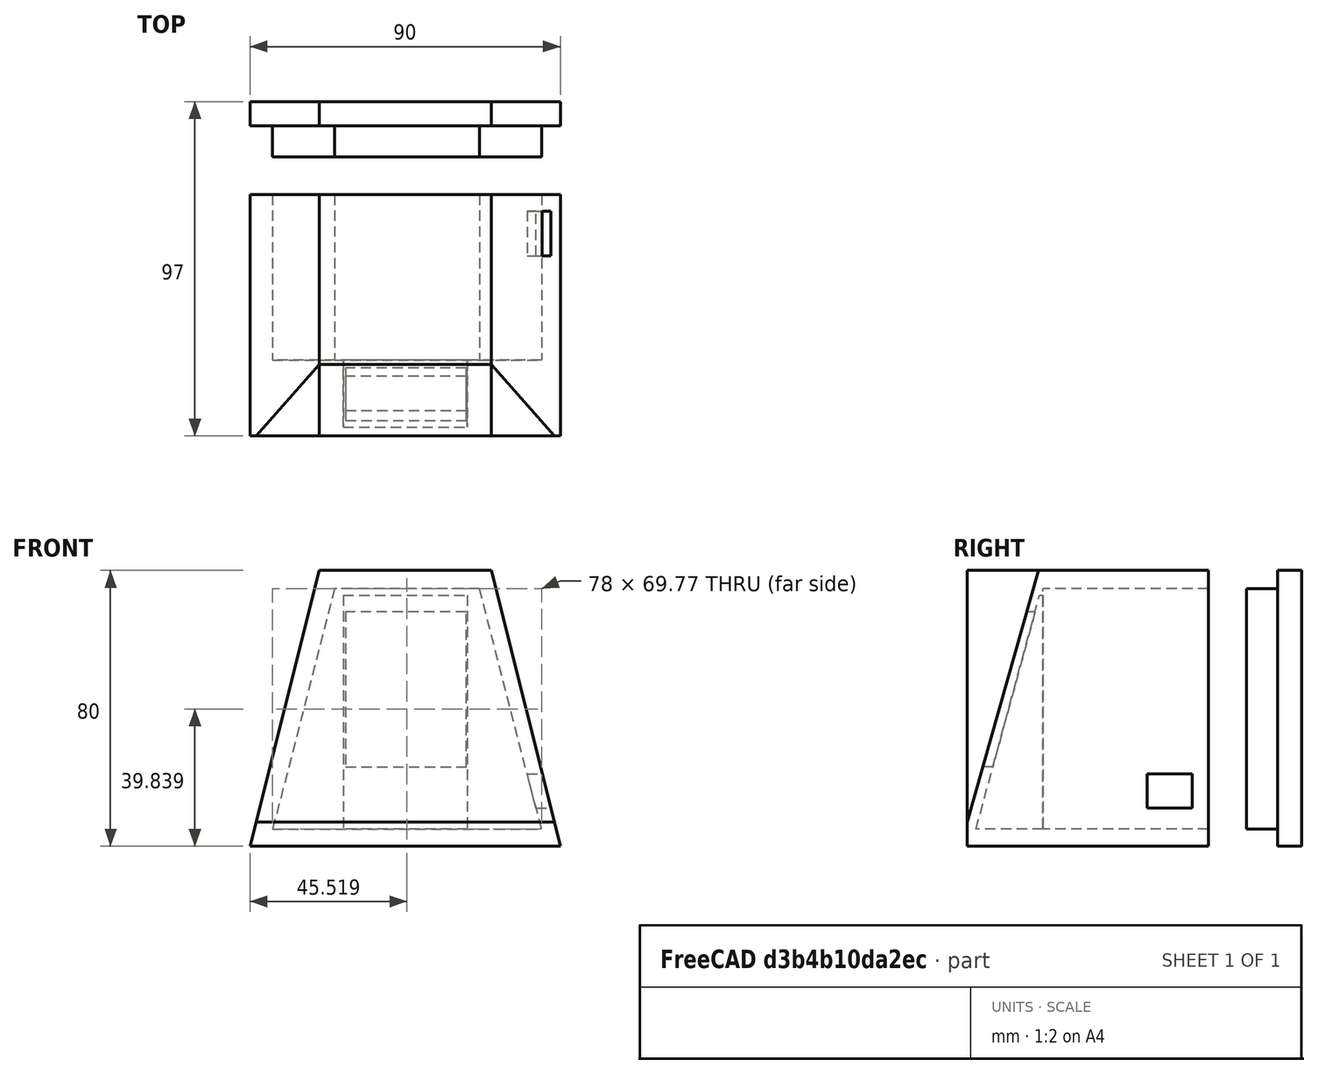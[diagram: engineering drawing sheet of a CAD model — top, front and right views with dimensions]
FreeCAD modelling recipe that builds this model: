
FCSTD DOCUMENT  (FreeCAD 0.19R24415 (Git))
Label: cad_1
License: All rights reserved
LicenseURL: http://en.wikipedia.org/wiki/All_rights_reserved
objects: Sketcher::SketchObject×8, Part::Extrusion×7, Part::Cut×6, Mesh::Feature×2, PartDesign::Pad×1, PartDesign::Body×1, Part::Fuse×1
note: 25 computed .brp shape members not serialized (recipe doc carries the construction recipe); baked Part::Feature solids carry a one-line shape summary decoded from their .brp

FEATURE [Sketcher::SketchObject] Sketch
  FullyConstrained = true
  MapMode = 5
  Placement = pos=(0,0,0) rot=(1,0,0;1.5708rad)
  Support = -> [XZ_Plane]
  sketch-geometry (4):
    g0: LineSegment StartX=0 StartY=0 StartZ=0 EndX=90 EndY=0 EndZ=0
    g1: LineSegment StartX=90 StartY=0 StartZ=0 EndX=70 EndY=80 EndZ=0
    g2: LineSegment StartX=70 StartY=80 StartZ=0 EndX=20 EndY=80 EndZ=0
    g3: LineSegment StartX=20 StartY=80 StartZ=0 EndX=0 EndY=0 EndZ=0
  constraints (11):
    c: Horizontal(g0)
    c: Coincident(g0,g1)
    c: Coincident(g1,g2)
    c: Horizontal(g2)
    c: Coincident(g2,g3)
    c: Coincident(g3,g0)
    c: Equal(g3,g1)
    c: DistanceX(g0,g0) = 90
    c: DistanceX(g2,g2) = 50
    c: Coincident(g0,g-1)
    c: DistanceY(g0,g1) = 80
FEATURE [PartDesign::Pad] Pad
  Direction = (1,1,1)
  Length = 70
  Length2 = 100
  Placement = pos=(0,0,0) rot=(1,0,0;1.5708rad)
  Profile = -> Sketch
  Refine = true
  Type = 0
FEATURE [PartDesign::Body] Body
  Group = -> [Sketch,Pad]
  Origin = -> Origin
  Tip = -> Pad
FEATURE [Sketcher::SketchObject] Sketch001
  FullyConstrained = true
  MapMode = 5
  Placement = pos=(0,0,0) rot=(0.57735,0.57735,0.57735;2.0944rad)
  Support = -> [YZ_Plane]
  sketch-geometry (4):
    g0: LineSegment StartX=-105 StartY=0 StartZ=0 EndX=-105 EndY=95 EndZ=0
    g1: LineSegment StartX=-105 StartY=95 StartZ=0 EndX=-45 EndY=95 EndZ=0
    g2: LineSegment StartX=-45 StartY=95 StartZ=0 EndX=-72 EndY=0 EndZ=0
    g3: LineSegment StartX=-72 StartY=0 StartZ=0 EndX=-105 EndY=0 EndZ=0
  constraints (12):
    c: PointOnObject(g0,g-1)
    c: Vertical(g0)
    c: Coincident(g0,g1)
    c: Horizontal(g1)
    c: Coincident(g1,g2)
    c: PointOnObject(g2,g-1)
    c: Coincident(g2,g3)
    c: Coincident(g3,g0)
    c: DistanceX(g0,g-1) = 105
    c: DistanceX(g1,g1) = 60
    c: DistanceX(g3,g3) = 33
    c: DistanceY(g0,g0) = 95
FEATURE [Part::Extrusion] Extrude
  Base = -> Sketch001
  Dir = (1,-1e-16,1e-16)
  DirMode = 2
  FaceMakerClass = Part::FaceMakerBullseye
  LengthFwd = 100
  LengthRev = 0
  Solid = true
  Symmetric = false
FEATURE [Part::Cut] Cut
  Base = -> Pad
  Refine = true
  Tool = -> Extrude
FEATURE [Sketcher::SketchObject] Sketch002
  FullyConstrained = false
  MapMode = 5
  Placement = pos=(0,0,0) rot=(1,0,0;1.5708rad)
  Support = -> [XZ_Plane]
  sketch-geometry (4):
    g0: LineSegment StartX=6.51919 StartY=4.95552 StartZ=0 EndX=24.5192 EndY=74.7219 EndZ=0
    g1: LineSegment StartX=24.5192 StartY=74.7219 StartZ=0 EndX=66.5192 EndY=74.7219 EndZ=0
    g2: LineSegment StartX=66.5192 StartY=74.7219 StartZ=0 EndX=84.5192 EndY=4.95552 EndZ=0
    g3: LineSegment StartX=84.5192 StartY=4.95552 StartZ=0 EndX=6.51919 EndY=4.95552 EndZ=0
  constraints (9):
    c: Coincident(g0,g1)
    c: Horizontal(g1)
    c: Coincident(g1,g2)
    c: Coincident(g2,g3)
    c: Coincident(g3,g0)
    c: Horizontal(g3)
    c: Equal(g2,g0)
    c: DistanceX(g3,g3) = 78
    c: DistanceX(g1,g1) = 42
FEATURE [Part::Extrusion] Extrude001
  Base = -> Sketch002
  Dir = (0,-1,2e-16)
  DirMode = 2
  FaceMakerClass = Part::FaceMakerBullseye
  LengthFwd = 100
  LengthRev = 0
  Placement = pos=(0,52,0) rot=(0,0,1;0rad)
  Solid = true
  Symmetric = false
FEATURE [Sketcher::SketchObject] Sketch003
  FullyConstrained = false
  MapMode = 5
  Placement = pos=(0,0,0) rot=(1,0,0;1.5708rad)
  sketch-geometry (4):
    g0: LineSegment StartX=6.51919 StartY=4.95552 StartZ=0 EndX=24.5192 EndY=74.7219 EndZ=0
    g1: LineSegment StartX=24.5192 StartY=74.7219 StartZ=0 EndX=66.5192 EndY=74.7219 EndZ=0
    g2: LineSegment StartX=66.5192 StartY=74.7219 StartZ=0 EndX=84.5192 EndY=4.95552 EndZ=0
    g3: LineSegment StartX=84.5192 StartY=4.95552 StartZ=0 EndX=6.51919 EndY=4.95552 EndZ=0
  constraints (9):
    c: Coincident(g0,g1)
    c: Horizontal(g1)
    c: Coincident(g1,g2)
    c: Coincident(g2,g3)
    c: Coincident(g3,g0)
    c: Horizontal(g3)
    c: Equal(g2,g0)
    c: DistanceX(g3,g3) = 78
    c: DistanceX(g1,g1) = 42
FEATURE [Part::Extrusion] Extrude002  label="deckel"
  Base = -> Sketch003
  Dir = (0,-1,2e-16)
  DirMode = 2
  FaceMakerClass = Part::FaceMakerBullseye
  LengthFwd = 15
  LengthRev = 0
  Placement = pos=(0,26,0) rot=(0,0,1;0rad)
  Solid = true
  Symmetric = false
FEATURE [Part::Cut] Cut001
  Base = -> Cut
  Refine = true
  Tool = -> Extrude001
FEATURE [Sketcher::SketchObject] Sketch004
  FullyConstrained = false
  MapMode = 5
  Placement = pos=(0,0,0) rot=(1,0,0;1.5708rad)
  Support = -> [XZ_Plane]
  sketch-geometry (7):
    g0: LineSegment StartX=27.6692 StartY=23.0204 StartZ=0 EndX=62.6692 EndY=23.0204 EndZ=0
    g1: LineSegment StartX=62.6692 StartY=23.0204 StartZ=0 EndX=62.6692 EndY=68.0204 EndZ=0
    g2: LineSegment StartX=62.6692 StartY=68.0204 StartZ=0 EndX=27.6692 EndY=68.0204 EndZ=0
    g3: LineSegment StartX=27.6692 StartY=68.0204 StartZ=0 EndX=27.6692 EndY=23.0204 EndZ=0
    g4: LineSegment StartX=20.1692 StartY=99.6457 StartZ=0 EndX=20.1692 EndY=-18.0291 EndZ=0
    g5: LineSegment StartX=70.1692 StartY=99.3523 StartZ=0 EndX=70.1692 EndY=-16.049 EndZ=0
    g6: LineSegment StartX=10.275 StartY=80.0204 StartZ=0 EndX=94.2286 EndY=80.0204 EndZ=0
  constraints (16):
    c: Coincident(g0,g1)
    c: Coincident(g1,g2)
    c: Coincident(g2,g3)
    c: Coincident(g3,g0)
    c: Horizontal(g0)
    c: Horizontal(g2)
    c: Vertical(g1)
    c: Vertical(g3)
    c: DistanceY(g1,g1) = 45
    c: DistanceX(g2,g2) = 35
    c: Vertical(g4)
    c: Vertical(g5)
    c: DistanceX(g4,g5) = 50
    c: DistanceX(g1,g5) = 7.5
    c: Horizontal(g6)
    c: DistanceY(g1,g6) = 12
FEATURE [Part::Extrusion] Extrude003
  Base = -> Sketch004
  Dir = (0,-1,2e-16)
  DirMode = 2
  FaceMakerClass = Part::FaceMakerBullseye
  LengthFwd = 100
  LengthRev = 0
  Solid = true
  Symmetric = false
FEATURE [Part::Cut] Cut002
  Base = -> Cut001
  Refine = true
  Tool = -> Extrude003
FEATURE [Sketcher::SketchObject] Sketch005
  FullyConstrained = false
  MapMode = 5
  Placement = pos=(0,0,0) rot=(0.57735,0.57735,0.57735;2.0944rad)
  Support = -> [YZ_Plane]
  sketch-geometry (4):
    g0: LineSegment StartX=-43.7989 StartY=5.03269 StartZ=0 EndX=-67.422 EndY=5.03269 EndZ=0
    g1: LineSegment StartX=-67.422 StartY=5.03269 StartZ=0 EndX=-48.981 EndY=72.8159 EndZ=0
    g2: LineSegment StartX=-48.981 StartY=72.8159 StartZ=0 EndX=-43.7989 EndY=72.8159 EndZ=0
    g3: LineSegment StartX=-43.7989 StartY=72.8159 StartZ=0 EndX=-43.7989 EndY=5.03269 EndZ=0
  constraints (7):
    c: Horizontal(g0)
    c: Coincident(g0,g1)
    c: Coincident(g1,g2)
    c: Coincident(g2,g3)
    c: Coincident(g3,g0)
    c: Vertical(g3)
    c: Horizontal(g2)
FEATURE [Part::Extrusion] Extrude004
  Base = -> Sketch005
  Dir = (1,-1e-16,1e-16)
  DirMode = 2
  FaceMakerClass = Part::FaceMakerBullseye
  LengthFwd = 36
  LengthRev = 0
  Placement = pos=(27,0,0) rot=(0,0,1;0rad)
  Solid = true
  Symmetric = false
FEATURE [Part::Cut] Cut003
  Base = -> Cut002
  Refine = true
  Tool = -> Extrude004
FEATURE [Sketcher::SketchObject] Sketch006
  FullyConstrained = false
  MapMode = 5
  Placement = pos=(0,0,0) rot=(0.57735,0.57735,0.57735;2.0944rad)
  Support = -> [YZ_Plane]
  sketch-geometry (4):
    g0: LineSegment StartX=-27.7471 StartY=21.0472 StartZ=0 EndX=-14.7471 EndY=21.0472 EndZ=0
    g1: LineSegment StartX=-14.7471 StartY=21.0472 StartZ=0 EndX=-14.7471 EndY=11.0472 EndZ=0
    g2: LineSegment StartX=-14.7471 StartY=11.0472 StartZ=0 EndX=-27.7471 EndY=11.0472 EndZ=0
    g3: LineSegment StartX=-27.7471 StartY=11.0472 StartZ=0 EndX=-27.7471 EndY=21.0472 EndZ=0
  constraints (10):
    c: Coincident(g0,g1)
    c: Coincident(g1,g2)
    c: Coincident(g2,g3)
    c: Coincident(g3,g0)
    c: Horizontal(g0)
    c: Horizontal(g2)
    c: Vertical(g1)
    c: Vertical(g3)
    c: DistanceX(g0,g0) = 13
    c: DistanceY(g1,g1) = 10
FEATURE [Part::Extrusion] Extrude005
  Base = -> Sketch006
  Dir = (1,-1e-16,1e-16)
  DirMode = 2
  FaceMakerClass = Part::FaceMakerBullseye
  LengthFwd = 30
  LengthRev = 0
  Placement = pos=(70,10,0) rot=(0,0,1;0rad)
  Solid = true
  Symmetric = false
FEATURE [Part::Cut] Cut004
  Base = -> Cut003
  Refine = true
  Tool = -> Extrude005
FEATURE [Part::Cut] Cut005
  Base = -> Cut003
  Refine = true
  Tool = -> Extrude005
FEATURE [Mesh::Feature] Mesh  label="Cut004 (Meshed)"
FEATURE [Sketcher::SketchObject] Sketch007
  FullyConstrained = false
  MapMode = 5
  Placement = pos=(0,20,-4.4e-15) rot=(0,0.707107,0.707107;3.14159rad)
  sketch-geometry (4):
    g0: LineSegment StartX=-90 StartY=0 StartZ=0 EndX=-69.9991 EndY=80.0002 EndZ=0
    g1: LineSegment StartX=-69.9991 StartY=80.0002 StartZ=0 EndX=-19.9991 EndY=80.0002 EndZ=0
    g2: LineSegment StartX=-19.9991 StartY=80.0002 StartZ=0 EndX=0 EndY=0 EndZ=0
    g3: LineSegment StartX=0 StartY=0 StartZ=0 EndX=-90 EndY=0 EndZ=0
  constraints (8):
    c: Coincident(g0,g1)
    c: Coincident(g1,g2)
    c: Coincident(g2,g-1)
    c: Coincident(g2,g3)
    c: Coincident(g3,g0)
    c: DistanceX(g3,g3) = 90
    c: Horizontal(g1)
    c: DistanceX(g1,g1) = 50
FEATURE [Part::Extrusion] Extrude006
  Base = -> Sketch007
  Dir = (0,1,-2e-16)
  DirMode = 2
  FaceMakerClass = Part::FaceMakerBullseye
  LengthFwd = 7
  LengthRev = 0
  Solid = true
  Symmetric = false
FEATURE [Part::Fuse] Fusion
  Base = -> Extrude002
  Refine = true
  Tool = -> Extrude006
FEATURE [Mesh::Feature] Mesh001  label="Fusion (Meshed)"
